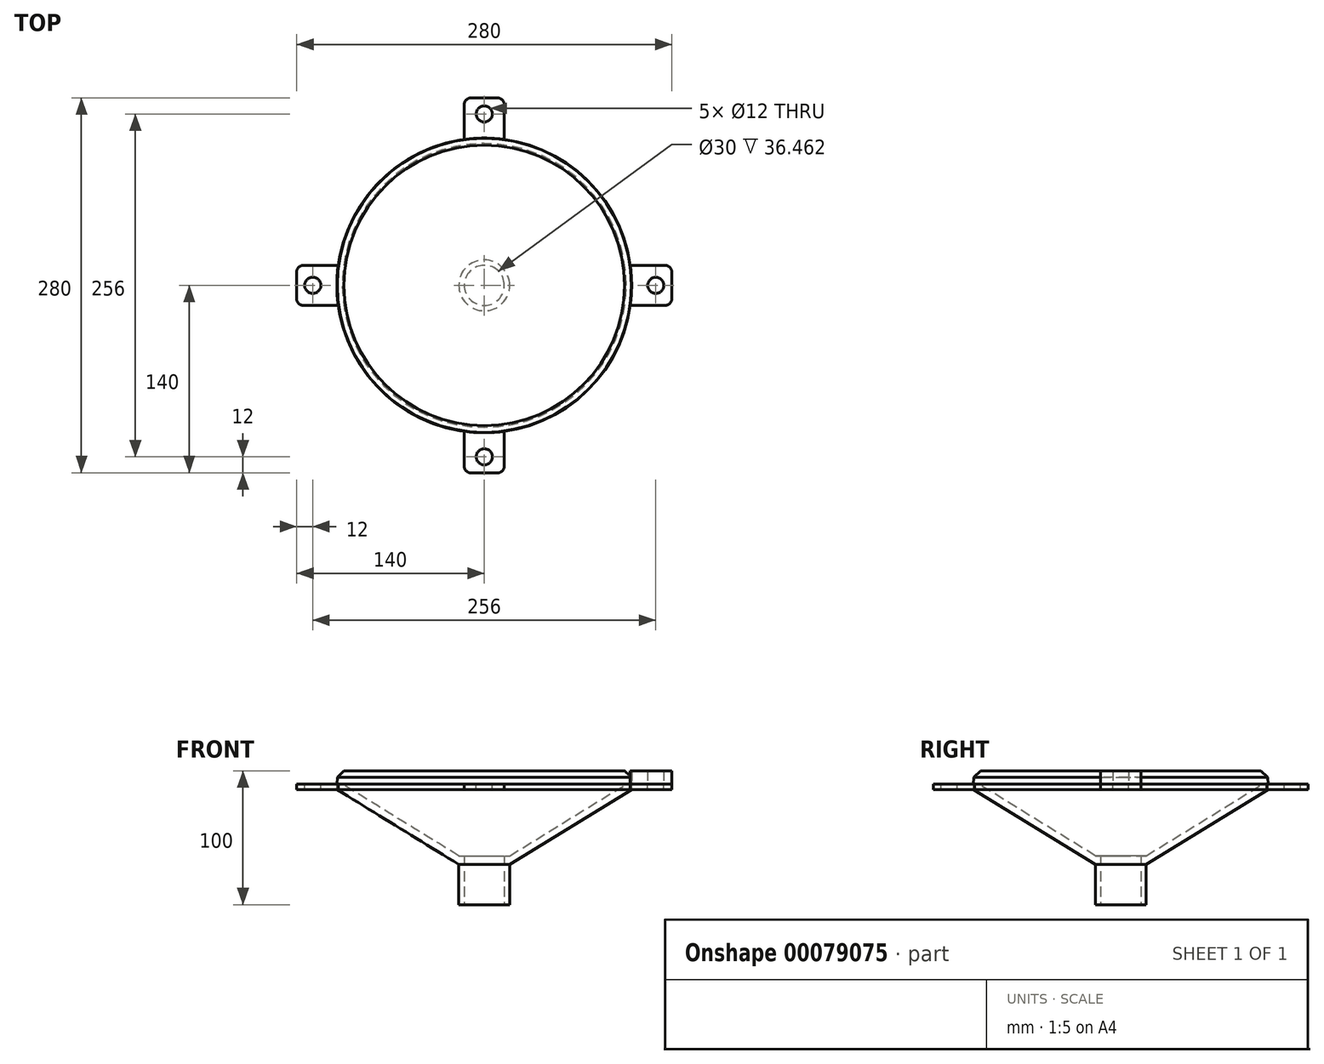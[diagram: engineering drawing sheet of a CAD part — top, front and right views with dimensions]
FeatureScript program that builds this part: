
annotation { "Feature Type Name" : "Feature", "Feature Type Description" : "" }
export const myFeature = defineFeature(function(context is Context, id is Id, definition is map)
    precondition{}
    {
        {
            var Q0;
            Q0=qCreatedBy(makeId("Front.planeOp"),FACE);
            var sketch = newSketch(context, id + "F0", { "sketchPlane" : qUnion([Q0])});
            skLineSegment(sketch, "E0", {"start": v(110, 86) * mm, "end": v(19, 30) * mm});
            skLineSegment(sketch, "E1", {"start": v(19, 30) * mm, "end": v(19, 0) * mm});
            skLineSegment(sketch, "E2", {"start": v(19, 0) * mm, "end": v(15, 0) * mm});
            skLineSegment(sketch, "E3", {"start": v(110, 86) * mm, "end": v(110, 90) * mm});
            skLineSegment(sketch, "E4", {"start": v(110, 90) * mm, "end": v(106, 90) * mm});
            skLineSegment(sketch, "E5", {"start": v(106, 90) * mm, "end": v(19, 36.46) * mm});
            skLineSegment(sketch, "E6", {"start": v(19, 36.46) * mm, "end": v(15, 36.46) * mm});
            skLineSegment(sketch, "E7", {"start": v(15, 36.46) * mm, "end": v(15, 0) * mm});
            skPoint(sketch, "E8.orphan", {"position": v(0, 0) * mm});
            skLineSegment(sketch, "E9", {"start": v(0, 0) * mm, "end": v(0, 36.46) * mm});
            skSolve(sketch);
        }
        {
            var Q0;
            Q0 = qSketchRegion(id + "F0", true);
            var Q1;
            Q1=sQuery(id+"F0.wireOp",EDGE,"E9");
            revolve(context, id + "F1", {"entities" : qUnion([Q0]), "axis" : qUnion([Q1]), "revolveType" : RevolveType.FULL});
        }
        {
            var Q0;
            Q0=makeQuery(id+"F1.opRevolve","SWEPT_FACE",FACE,{"disambiguationData":[OSD([sQuery(id+"F0.wireOp",EDGE,"E4")])]});
            var sketch = newSketch(context, id + "F2", { "sketchPlane" : qUnion([Q0])});
            skLineSegment(sketch, "E10", {"start": v(110, 0) * mm, "end": v(140, 0) * mm, "construction": true});
            skArc(sketch, "E11.0", {"start": v(108.97, -15) * mm, "mid": v(110, 0) * mm, "end": v(108.97, 15) * mm});
            skLineSegment(sketch, "E12", {"start": v(108.97, 15) * mm, "end": v(135, 15) * mm});
            skLineSegment(sketch, "E13", {"start": v(140, 10) * mm, "end": v(140, -10) * mm});
            skLineSegment(sketch, "E14", {"start": v(135, -15) * mm, "end": v(108.97, -15) * mm});
            skPoint(sketch, "E15.visualSharp", {"position": v(140, 15) * mm});
            skArc(sketch, "E15.filletArc", {"start": v(140, 10) * mm, "mid": v(138.54, 13.54) * mm, "end": v(135, 15) * mm});
            skPoint(sketch, "E16.visualSharp", {"position": v(140, -15) * mm});
            skArc(sketch, "E16.filletArc", {"start": v(135, -15) * mm, "mid": v(138.54, -13.54) * mm, "end": v(140, -10) * mm});
            skCircle(sketch, "E17", {"center": v(128, 0) * mm, "radius": 6 * mm});
            skSolve(sketch);
        }
        {
            var Q0;
            Q0 = qSketchRegion(id + "F2", true);
            var Q1;
            Q1=makeQuery(id+"F1.opRevolve","SWEPT_FACE",FACE,{"disambiguationData":[OSD([sQuery(id+"F0.wireOp",EDGE,"E0")])]});
            extrude(context, id + "F3", {"entities" : qUnion([Q0]), "oppositeDirection" : true, "endBoundEntityFace" : qUnion([Q1]), "depth" : 4 * mm});
        }
        {
            var Q0;
            Q0=makeQuery(id+"F3.opExtrude","SWEPT_BODY",BODY,{"disambiguationData":[OSD([sQuery(id+"F2.wireOp",EDGE,"E11.0"),sQuery(id+"F2.wireOp",EDGE,"E12"),sQuery(id+"F2.wireOp",EDGE,"E13"),sQuery(id+"F2.wireOp",EDGE,"E14"),sQuery(id+"F2.wireOp",EDGE,"E15.filletArc"),sQuery(id+"F2.wireOp",EDGE,"E16.filletArc"),sQuery(id+"F2.wireOp",EDGE,"E17")])]});
            var Q1;
            Q1=makeQuery(id+"F1.opRevolve","SWEPT_FACE",FACE,{"disambiguationData":[OSD([sQuery(id+"F0.wireOp",EDGE,"E7")])]});
            circularPattern(context, id + "F4", {"entities" : qUnion([Q0]), "axis" : qUnion([Q1]), "angle" : 360 * degree, "instanceCount" : 4, "equalSpace" : true});
        }
        {
            var Q0;
            Q0=makeQuery(id+"F3.opExtrude","CAP_FACE",FACE,{"disambiguationData":[OSD([sQuery(id+"F2.wireOp",EDGE,"E11.0"),sQuery(id+"F2.wireOp",EDGE,"E12"),sQuery(id+"F2.wireOp",EDGE,"E13"),sQuery(id+"F2.wireOp",EDGE,"E14"),sQuery(id+"F2.wireOp",EDGE,"E15.filletArc"),sQuery(id+"F2.wireOp",EDGE,"E16.filletArc"),sQuery(id+"F2.wireOp",EDGE,"E17")])],"isStart":true});
            var sketch = newSketch(context, id + "F8", { "sketchPlane" : qUnion([Q0])});
            skCircle(sketch, "E18", {"center": v(0, 0) * mm, "radius": 110 * mm});
            skSolve(sketch);
        }
        {
            var Q0;
            Q0 = qSketchRegion(id + "F8", true);
            extrude(context, id + "F9", {"entities" : qUnion([Q0]), "depth" : 10 * mm, "hasDraft" : true, "draftAngle" : 3 * degree, "draftPullDirection" : true});
        }
        {
            var Q0;
            Q0=makeQuery(id+"F9.opExtrude","CAP_EDGE",EDGE,{"disambiguationData":[OSD([sQuery(id+"F8.wireOp",EDGE,"E18")])],"isStart":false});
            chamfer(context, id + "F5", {"entities" : qUnion([Q0]), "width" : 5 * mm, "tangentPropagation" : true});
        }
        {
            var Q0;
            Q0=makeQuery(id+"F3.opExtrude","CAP_FACE",FACE,{"disambiguationData":[OSD([sQuery(id+"F2.wireOp",EDGE,"E11.0"),sQuery(id+"F2.wireOp",EDGE,"E12"),sQuery(id+"F2.wireOp",EDGE,"E13"),sQuery(id+"F2.wireOp",EDGE,"E14"),sQuery(id+"F2.wireOp",EDGE,"E15.filletArc"),sQuery(id+"F2.wireOp",EDGE,"E16.filletArc"),sQuery(id+"F2.wireOp",EDGE,"E17")])],"isStart":true});
            var sketch = newSketch(context, id + "F6", { "sketchPlane" : qUnion([Q0])});
            skLineSegment(sketch, "E19.0", {"start": v(135, -15) * mm, "end": v(108.97, -15) * mm});
            skArc(sketch, "E20.0", {"start": v(135, -15) * mm, "mid": v(138.54, -13.54) * mm, "end": v(140, -10) * mm});
            skLineSegment(sketch, "E21.0", {"start": v(140, 10) * mm, "end": v(140, -10) * mm});
            skArc(sketch, "E22.0", {"start": v(140, 10) * mm, "mid": v(138.54, 13.54) * mm, "end": v(135, 15) * mm});
            skLineSegment(sketch, "E23.0", {"start": v(108.97, 15) * mm, "end": v(135, 15) * mm});
            skArc(sketch, "E24.0", {"start": v(108.97, 15) * mm, "mid": v(110, 0) * mm, "end": v(108.97, -15) * mm});
            skCircle(sketch, "E25.0", {"center": v(128, 0) * mm, "radius": 6 * mm});
            skSolve(sketch);
        }
        {
            var Q0;
            Q0=makeQuery(id+"F6.imprint","IMPRINT",FACE,{"disambiguationData":[TD([[makeQuery(id+"F6.imprint","IMPRINT",EDGE,{"derivedFrom":sQuery(id+"F6.wireOp",EDGE,"E19.0")}),-1.0]])]});
            extrude(context, id + "F7", {"entities" : qUnion([Q0]), "depth" : 10 * mm});
        }
    });
